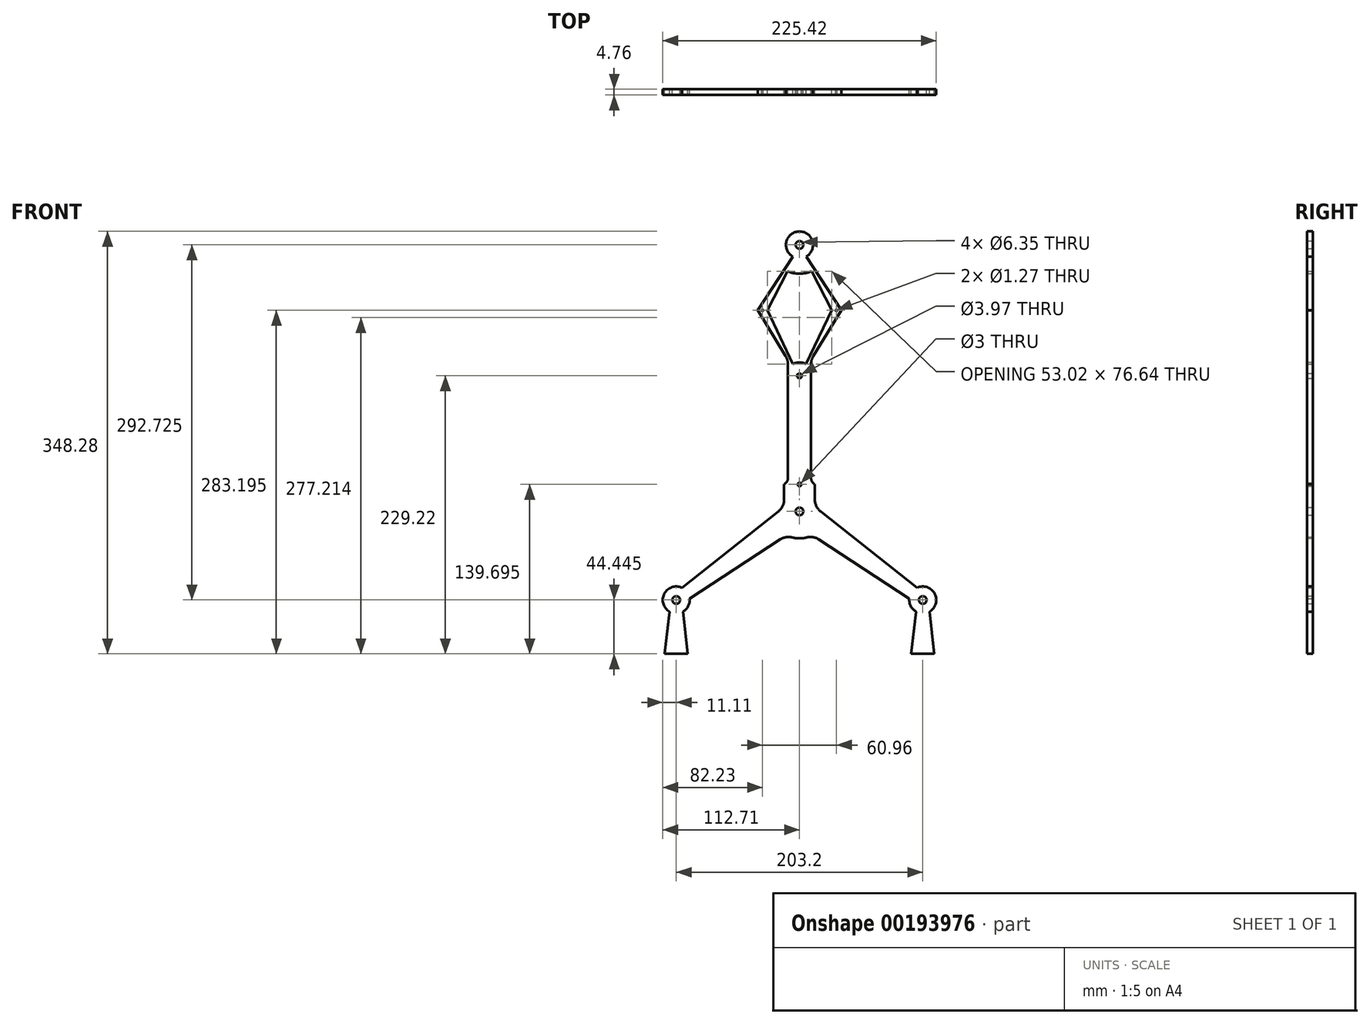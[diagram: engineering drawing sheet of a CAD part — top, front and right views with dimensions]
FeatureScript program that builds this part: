
annotation { "Feature Type Name" : "Feature", "Feature Type Description" : "" }
export const myFeature = defineFeature(function(context is Context, id is Id, definition is map)
    precondition{}
    {
        {
            var Q0;
            Q0=qCreatedBy(makeId("Front.planeOp"),FACE);
            var sketch = newSketch(context, id + "F0", { "sketchPlane" : qUnion([Q0])});
            skLineSegment(sketch, "E0", {"start": v(-111.13, -117.48) * mm, "end": v(-107.16, -82.65) * mm});
            skLineSegment(sketch, "E1", {"start": v(-92.08, -117.48) * mm, "end": v(-96.04, -82.65) * mm});
            skLineSegment(sketch, "E2", {"start": v(-101.6, -73.03) * mm, "end": v(-101.6, -117.48) * mm, "construction": true});
            skLineSegment(sketch, "E3", {"start": v(-97.03, -62.9) * mm, "end": v(-17.54, -0.21) * mm});
            skLineSegment(sketch, "E4", {"start": v(-15.87, -23.13) * mm, "end": v(-90.54, -71.92) * mm});
            skLineSegment(sketch, "E5", {"start": v(97.03, -62.9) * mm, "end": v(17.54, -0.21) * mm});
            skLineSegment(sketch, "E6", {"start": v(90.54, -71.92) * mm, "end": v(15.87, -23.13) * mm});
            skLineSegment(sketch, "E7", {"start": v(-97.03, -62.9) * mm, "end": v(-90.54, -71.92) * mm, "construction": true});
            skLineSegment(sketch, "E8", {"start": v(-101.6, -117.48) * mm, "end": v(101.6, -117.48) * mm, "construction": true});
            skLineSegment(sketch, "E9", {"start": v(-12.7, 9.76) * mm, "end": v(-12.7, 22.22) * mm});
            skLineSegment(sketch, "E10", {"start": v(12.7, 9.76) * mm, "end": v(12.7, 22.23) * mm});
            skLineSegment(sketch, "E11", {"start": v(0, 230.81) * mm, "end": v(0, -117.48) * mm, "construction": true});
            skLineSegment(sketch, "E12", {"start": v(0, 0) * mm, "end": v(-101.6, -73.03) * mm, "construction": true});
            skLineSegment(sketch, "E13", {"start": v(0, 0) * mm, "end": v(101.6, -73.03) * mm, "construction": true});
            skLineSegment(sketch, "E14", {"start": v(97.03, -62.9) * mm, "end": v(90.54, -71.92) * mm, "construction": true});
            skLineSegment(sketch, "E15", {"start": v(-9.52, 121.43) * mm, "end": v(-9.52, 27.72) * mm});
            skLineSegment(sketch, "E16", {"start": v(9.52, 121.43) * mm, "end": v(9.52, 27.72) * mm});
            skArc(sketch, "E17", {"start": v(-12.7, 22.22) * mm, "mid": v(-10.38, 24.55) * mm, "end": v(-9.52, 27.72) * mm});
            skArc(sketch, "E18", {"start": v(9.52, 27.72) * mm, "mid": v(10.38, 24.55) * mm, "end": v(12.7, 22.22) * mm});
            skLineSegment(sketch, "E19", {"start": v(-11.4, 128.06) * mm, "end": v(-34.45, 165.73) * mm});
            skLineSegment(sketch, "E20", {"start": v(-34.45, 165.73) * mm, "end": v(-5.56, 210.08) * mm});
            skLineSegment(sketch, "E21", {"start": v(11.4, 128.06) * mm, "end": v(34.45, 165.73) * mm});
            skLineSegment(sketch, "E22", {"start": v(34.45, 165.73) * mm, "end": v(5.56, 210.08) * mm});
            skArc(sketch, "E23", {"start": v(-9.52, 121.43) * mm, "mid": v(-10, 124.87) * mm, "end": v(-11.4, 128.06) * mm});
            skArc(sketch, "E24", {"start": v(11.4, 128.06) * mm, "mid": v(10, 124.87) * mm, "end": v(9.52, 121.43) * mm});
            skLineSegment(sketch, "E25", {"start": v(-9.94, 198.06) * mm, "end": v(-26.51, 165.73) * mm});
            skLineSegment(sketch, "E26", {"start": v(-26.51, 165.73) * mm, "end": v(-5.46, 121.43) * mm});
            skLineSegment(sketch, "E27", {"start": v(5.46, 121.43) * mm, "end": v(26.51, 165.73) * mm});
            skLineSegment(sketch, "E28", {"start": v(26.51, 165.73) * mm, "end": v(9.94, 198.06) * mm});
            skLineSegment(sketch, "E29", {"start": v(-5.56, 210.08) * mm, "end": v(5.56, 210.08) * mm, "construction": true});
            skLineSegment(sketch, "E30", {"start": v(-107.16, -82.65) * mm, "end": v(-96.04, -82.65) * mm, "construction": true});
            skPoint(sketch, "E31", {"position": v(-101.6, -82.65) * mm});
            skLineSegment(sketch, "E32", {"start": v(-111.13, -117.48) * mm, "end": v(-92.08, -117.48) * mm});
            skPoint(sketch, "E33", {"position": v(-101.6, -117.48) * mm});
            skLineSegment(sketch, "E34", {"start": v(92.08, -117.48) * mm, "end": v(96.04, -82.65) * mm});
            skLineSegment(sketch, "E35", {"start": v(111.12, -117.48) * mm, "end": v(107.16, -82.65) * mm});
            skLineSegment(sketch, "E36", {"start": v(101.6, -73.03) * mm, "end": v(101.6, -117.48) * mm, "construction": true});
            skLineSegment(sketch, "E37", {"start": v(96.04, -82.65) * mm, "end": v(107.16, -82.65) * mm, "construction": true});
            skPoint(sketch, "E38", {"position": v(101.6, -82.65) * mm});
            skLineSegment(sketch, "E39", {"start": v(92.08, -117.48) * mm, "end": v(111.12, -117.48) * mm});
            skPoint(sketch, "E40", {"position": v(101.6, -117.48) * mm});
            skCircle(sketch, "E41", {"center": v(101.6, -73.03) * mm, "radius": 11.11 * mm});
            skCircle(sketch, "E42", {"center": v(-101.6, -73.03) * mm, "radius": 11.11 * mm});
            skPoint(sketch, "E43", {"position": v(-93.79, -67.4) * mm});
            skPoint(sketch, "E44", {"position": v(93.79, -67.4) * mm});
            skLineSegment(sketch, "E45", {"start": v(-15.87, -23.13) * mm, "end": v(-26.99, -7.67) * mm, "construction": true});
            skPoint(sketch, "E46", {"position": v(-21.43, -15.4) * mm});
            skLineSegment(sketch, "E47", {"start": v(15.87, -23.13) * mm, "end": v(26.99, -7.67) * mm, "construction": true});
            skPoint(sketch, "E48", {"position": v(21.43, -15.4) * mm});
            skArc(sketch, "E49", {"start": v(-5.68, -21.49) * mm, "mid": v(0, -22.22) * mm, "end": v(5.68, -21.49) * mm});
            skPoint(sketch, "E50", {"position": v(0, -22.23) * mm});
            skPoint(sketch, "E50.positionSnap0", {"position": v(0, -22.23) * mm});
            skArc(sketch, "E51", {"start": v(-5.68, -21.49) * mm, "mid": v(-10.95, -21.23) * mm, "end": v(-15.87, -23.13) * mm});
            skArc(sketch, "E52", {"start": v(15.87, -23.13) * mm, "mid": v(10.95, -21.23) * mm, "end": v(5.68, -21.49) * mm});
            skArc(sketch, "E53", {"start": v(12.7, 9.76) * mm, "mid": v(13.97, 4.22) * mm, "end": v(17.54, -0.21) * mm});
            skArc(sketch, "E54", {"start": v(-17.54, -0.21) * mm, "mid": v(-13.97, 4.22) * mm, "end": v(-12.7, 9.76) * mm});
            skLineSegment(sketch, "E55", {"start": v(-12.7, 22.22) * mm, "end": v(12.7, 22.22) * mm, "construction": true});
            skPoint(sketch, "E56", {"position": v(0, 22.22) * mm});
            skLineSegment(sketch, "E57", {"start": v(-9.52, 27.72) * mm, "end": v(9.52, 27.72) * mm, "construction": true});
            skPoint(sketch, "E58", {"position": v(0, 27.72) * mm});
            skLineSegment(sketch, "E59", {"start": v(-34.45, 165.73) * mm, "end": v(34.45, 165.73) * mm, "construction": true});
            skPoint(sketch, "E60", {"position": v(0, 111.75) * mm});
            skArc(sketch, "E61", {"start": v(5.46, 121.43) * mm, "mid": v(0, 122.86) * mm, "end": v(-5.46, 121.43) * mm});
            skPoint(sketch, "E62", {"position": v(0, 122.86) * mm});
            skArc(sketch, "E63", {"start": v(-9.94, 198.06) * mm, "mid": v(0, 195.89) * mm, "end": v(9.94, 198.06) * mm});
            skPoint(sketch, "E64", {"position": v(0, 195.89) * mm});
            skPoint(sketch, "E65", {"position": v(0, 165.73) * mm});
            skPoint(sketch, "E66", {"position": v(0, 210.08) * mm});
            skCircle(sketch, "E67", {"center": v(0, 219.7) * mm, "radius": 11.11 * mm});
            skPoint(sketch, "E68", {"position": v(30.48, 165.73) * mm});
            skPoint(sketch, "E69", {"position": v(-30.48, 165.73) * mm});
            skLineSegment(sketch, "E70", {"start": v(0, 219.7) * mm, "end": v(-30.48, 165.73) * mm, "construction": true});
            skLineSegment(sketch, "E71", {"start": v(-30.48, 165.73) * mm, "end": v(0, 111.75) * mm, "construction": true});
            skLineSegment(sketch, "E72", {"start": v(0, 219.7) * mm, "end": v(30.48, 165.73) * mm, "construction": true});
            skLineSegment(sketch, "E73", {"start": v(30.48, 165.73) * mm, "end": v(0, 111.75) * mm, "construction": true});
            skLineSegment(sketch, "E74", {"start": v(-9.52, 121.43) * mm, "end": v(9.52, 121.43) * mm, "construction": true});
            skArc(sketch, "E75", {"start": v(10.92, 132.91) * mm, "mid": v(0, 135.56) * mm, "end": v(-10.92, 132.91) * mm, "construction": true});
            skLineSegment(sketch, "E76", {"start": v(-10.92, 132.91) * mm, "end": v(-14.36, 132.91) * mm, "construction": true});
            skLineSegment(sketch, "E77", {"start": v(-9.94, 198.06) * mm, "end": v(-13.38, 198.06) * mm, "construction": true});
            skLineSegment(sketch, "E78", {"start": v(9.94, 198.06) * mm, "end": v(13.38, 198.06) * mm, "construction": true});
            skCircle(sketch, "E79", {"center": v(-101.6, -73.03) * mm, "radius": 3.18 * mm});
            skCircle(sketch, "E80", {"center": v(101.6, -73.03) * mm, "radius": 3.18 * mm});
            skCircle(sketch, "E81", {"center": v(0, 219.7) * mm, "radius": 3.18 * mm});
            skCircle(sketch, "E82", {"center": v(0, 0) * mm, "radius": 3.18 * mm});
            skPoint(sketch, "E83", {"position": v(0, 230.81) * mm});
            skCircle(sketch, "E84", {"center": v(0, 22.22) * mm, "radius": 1.5 * mm});
            skCircle(sketch, "E85", {"center": v(0, 111.75) * mm, "radius": 1.98 * mm});
            skCircle(sketch, "E86", {"center": v(30.48, 165.73) * mm, "radius": 0.64 * mm});
            skCircle(sketch, "E87", {"center": v(-30.48, 165.73) * mm, "radius": 0.64 * mm});
            skSolve(sketch);
        }
        {
            var Q0;
            Q0 = qSketchRegion(id + "F0", true);
            extrude(context, id + "F1", {"entities" : qUnion([Q0]), "depth" : 4.76 * mm});
        }
    });
